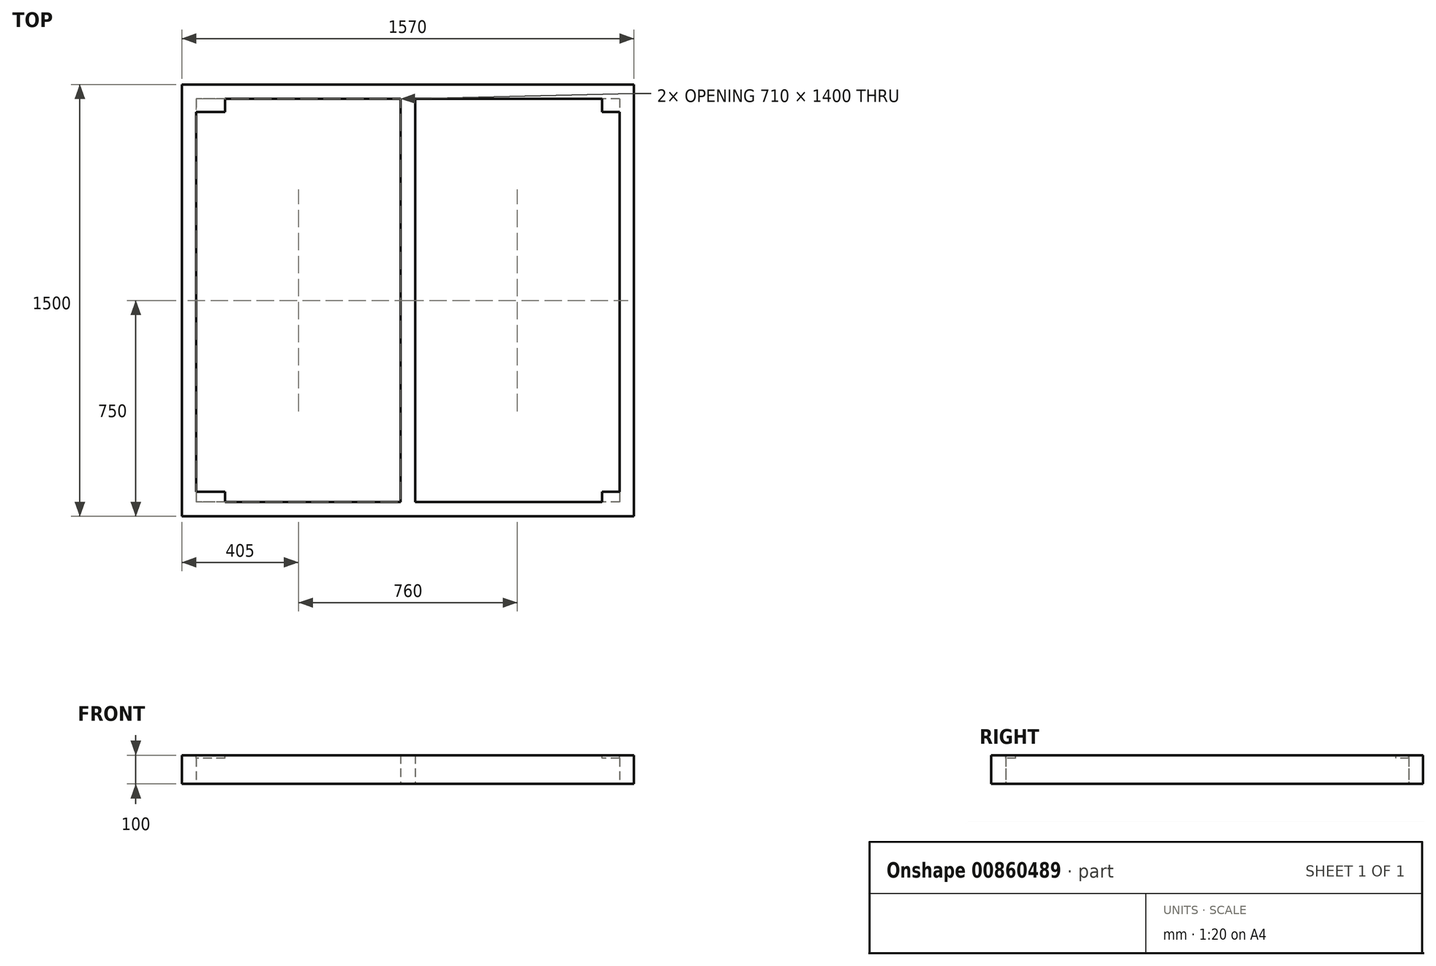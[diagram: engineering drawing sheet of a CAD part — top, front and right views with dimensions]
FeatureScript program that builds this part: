
annotation { "Feature Type Name" : "Feature", "Feature Type Description" : "" }
export const myFeature = defineFeature(function(context is Context, id is Id, definition is map)
    precondition{}
    {
        {
            var Q0;
            Q0=qCreatedBy(makeId("Top.planeOp"),FACE);
            var sketch = newSketch(context, id + "F0", { "sketchPlane" : qUnion([Q0])});
            skLineSegment(sketch, "E0.rect.bottom", {"start": v(785, 750) * mm, "end": v(-785, 750) * mm});
            skLineSegment(sketch, "E0.rect.top", {"start": v(785, -750) * mm, "end": v(-785, -750) * mm});
            skLineSegment(sketch, "E0.rect.left", {"start": v(785, 750) * mm, "end": v(785, -750) * mm});
            skLineSegment(sketch, "E0.rect.right", {"start": v(-785, 750) * mm, "end": v(-785, -750) * mm});
            skPoint(sketch, "E0.rect.middle", {"position": v(0, 0) * mm});
            skLineSegment(sketch, "E1.rect.bottom", {"start": v(735, 700) * mm, "end": v(25, 700) * mm});
            skLineSegment(sketch, "E1.rect.top", {"start": v(735, -700) * mm, "end": v(25, -700) * mm});
            skLineSegment(sketch, "E1.rect.left", {"start": v(735, 700) * mm, "end": v(735, -700) * mm});
            skLineSegment(sketch, "E1.rect.right", {"start": v(-735, 700) * mm, "end": v(-735, -700) * mm});
            skLineSegment(sketch, "E2.rect.left", {"start": v(25, 700) * mm, "end": v(25, -700) * mm});
            skLineSegment(sketch, "E2.rect.right", {"start": v(-25, 700) * mm, "end": v(-25, -700) * mm});
            skLineSegment(sketch, "E3.trimOffspring", {"start": v(-25, 700) * mm, "end": v(-735, 700) * mm});
            skLineSegment(sketch, "E4.trimOffspring", {"start": v(-25, -700) * mm, "end": v(-735, -700) * mm});
            skSolve(sketch);
        }
        {
            var Q0;
            Q0 = qSketchRegion(id + "F0", true);
            extrude(context, id + "F1", {"entities" : qUnion([Q0]), "depth" : 100 * mm, "offsetDistance" : 25 * mm});
        }
        {
            var Q0;
            Q0=makeQuery(id+"F1.opExtrude","CAP_FACE",FACE,{"disambiguationData":[OSD([sQuery(id+"F0.wireOp",EDGE,"E0.rect.bottom"),sQuery(id+"F0.wireOp",EDGE,"E0.rect.top"),sQuery(id+"F0.wireOp",EDGE,"E0.rect.left"),sQuery(id+"F0.wireOp",EDGE,"E0.rect.right"),sQuery(id+"F0.wireOp",EDGE,"E1.rect.bottom"),sQuery(id+"F0.wireOp",EDGE,"E1.rect.top"),sQuery(id+"F0.wireOp",EDGE,"E1.rect.left"),sQuery(id+"F0.wireOp",EDGE,"E1.rect.right"),sQuery(id+"F0.wireOp",EDGE,"E2.rect.left"),sQuery(id+"F0.wireOp",EDGE,"E2.rect.right"),sQuery(id+"F0.wireOp",EDGE,"E3.trimOffspring"),sQuery(id+"F0.wireOp",EDGE,"E4.trimOffspring")])],"isStart":false});
            var sketch = newSketch(context, id + "F2", { "sketchPlane" : qUnion([Q0])});
            skLineSegment(sketch, "E5.bottom", {"start": v(-735, 700) * mm, "end": v(-635, 700) * mm});
            skLineSegment(sketch, "E5.top", {"start": v(-735, 655) * mm, "end": v(-635, 655) * mm});
            skLineSegment(sketch, "E5.left", {"start": v(-735, 700) * mm, "end": v(-735, 655) * mm});
            skLineSegment(sketch, "E5.right", {"start": v(-635, 700) * mm, "end": v(-635, 655) * mm});
            skLineSegment(sketch, "E6.bottom", {"start": v(735, 700) * mm, "end": v(675, 700) * mm});
            skLineSegment(sketch, "E6.top", {"start": v(735, 655) * mm, "end": v(675, 655) * mm});
            skLineSegment(sketch, "E6.left", {"start": v(735, 700) * mm, "end": v(735, 655) * mm});
            skLineSegment(sketch, "E6.right", {"start": v(675, 700) * mm, "end": v(675, 655) * mm});
            skLineSegment(sketch, "E7.bottom", {"start": v(735, -700) * mm, "end": v(675, -700) * mm});
            skLineSegment(sketch, "E7.top", {"start": v(735, -665) * mm, "end": v(675, -665) * mm});
            skLineSegment(sketch, "E7.left", {"start": v(735, -700) * mm, "end": v(735, -665) * mm});
            skLineSegment(sketch, "E7.right", {"start": v(675, -700) * mm, "end": v(675, -665) * mm});
            skLineSegment(sketch, "E8.bottom", {"start": v(-735, -700) * mm, "end": v(-635, -700) * mm});
            skLineSegment(sketch, "E8.top", {"start": v(-735, -665) * mm, "end": v(-635, -665) * mm});
            skLineSegment(sketch, "E8.left", {"start": v(-735, -700) * mm, "end": v(-735, -665) * mm});
            skLineSegment(sketch, "E8.right", {"start": v(-635, -700) * mm, "end": v(-635, -665) * mm});
            skSolve(sketch);
        }
        {
            var Q0;
            Q0 = qSketchRegion(id + "F2", true);
            extrude(context, id + "F3", {"entities" : qUnion([Q0]), "operationType" : NewBodyOperationType.ADD, "oppositeDirection" : true, "depth" : 10 * mm, "offsetDistance" : 25 * mm});
        }
    });
